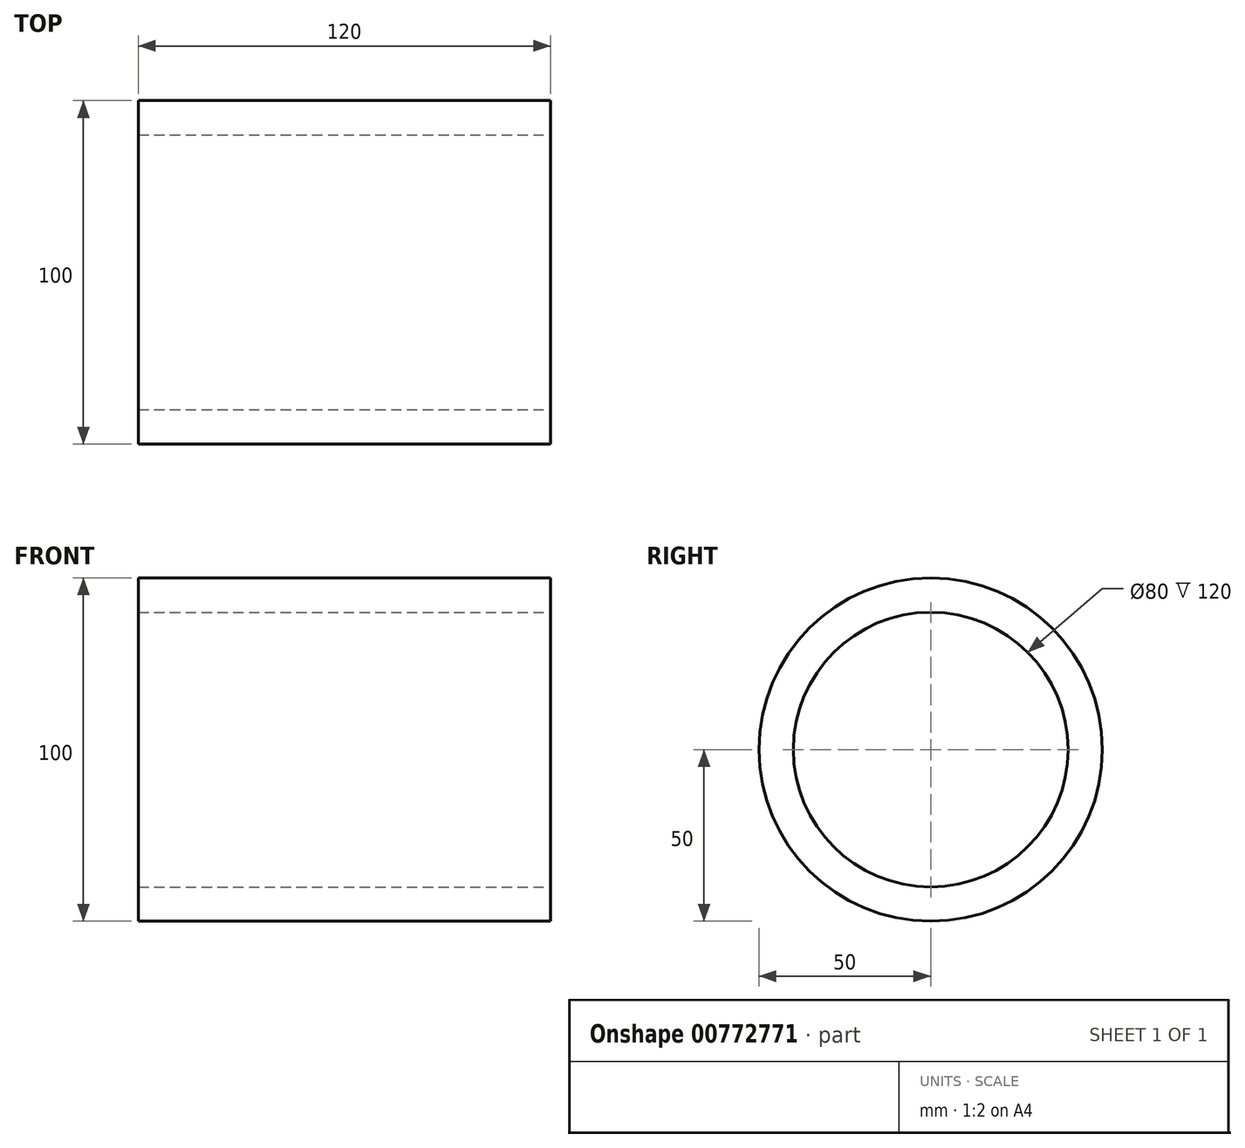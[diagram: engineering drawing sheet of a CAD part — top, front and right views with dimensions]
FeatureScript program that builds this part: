
annotation { "Feature Type Name" : "Feature", "Feature Type Description" : "" }
export const myFeature = defineFeature(function(context is Context, id is Id, definition is map)
    precondition{}
    {
        {
            var Q0;
            Q0=qCreatedBy(makeId("Right.planeOp"),FACE);
            var sketch = newSketch(context, id + "F0", { "sketchPlane" : qUnion([Q0])});
            skCircle(sketch, "E0", {"center": v(0, 0) * mm, "radius": 50 * mm});
            skSolve(sketch);
        }
        {
            var Q0;
            Q0 = qSketchRegion(id + "F0", true);
            extrude(context, id + "F1", {"entities" : qUnion([Q0]), "depth" : 120 * mm, "offsetDistance" : 25 * mm, "symmetric" : true});
        }
        {
            var Q0;
            Q0=makeQuery(id+"F1.opExtrude","CAP_FACE",FACE,{"disambiguationData":[OSD([sQuery(id+"F0.wireOp",EDGE,"E0")])],"isStart":false});
            var sketch = newSketch(context, id + "F2", { "sketchPlane" : qUnion([Q0])});
            skCircle(sketch, "E1", {"center": v(0, 0) * mm, "radius": 40 * mm});
            skSolve(sketch);
        }
        {
            var Q0;
            Q0=makeQuery(id+"F2.imprint","IMPRINT",FACE,{"disambiguationData":[TD([[makeQuery(id+"F2.imprint","IMPRINT",EDGE,{"derivedFrom":sQuery(id+"F2.wireOp",EDGE,"E1")}),1.0]])]});
            extrude(context, id + "F3", {"entities" : qUnion([Q0]), "operationType" : NewBodyOperationType.REMOVE, "endBound" : BoundingType.THROUGH_ALL, "oppositeDirection" : true, "depth" : 25 * mm, "offsetDistance" : 25 * mm});
        }
    });
